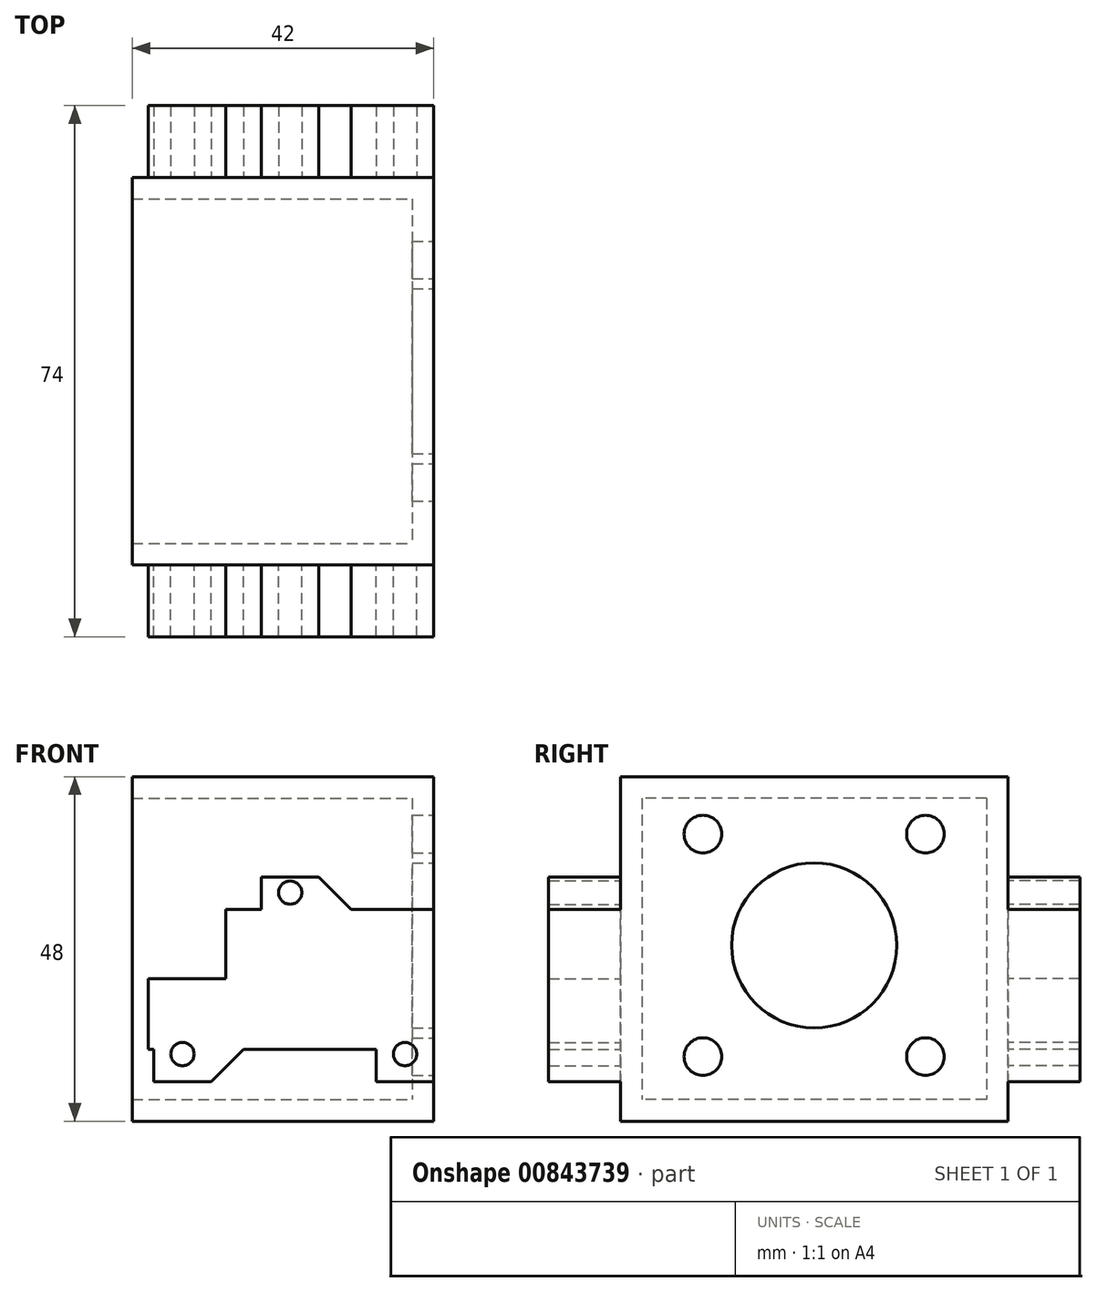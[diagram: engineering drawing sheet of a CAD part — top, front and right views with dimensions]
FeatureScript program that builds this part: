
annotation { "Feature Type Name" : "Feature", "Feature Type Description" : "" }
export const myFeature = defineFeature(function(context is Context, id is Id, definition is map)
    precondition{}
    {
        {
            var Q0;
            Q0=qCreatedBy(makeId("Front.planeOp"),FACE);
            var sketch = newSketch(context, id + "F0", { "sketchPlane" : qUnion([Q0])});
            skCircle(sketch, "E0", {"center": v(-1, 9.35) * mm, "radius": 1.63 * mm});
            skCircle(sketch, "E1", {"center": v(-32, 9.35) * mm, "radius": 1.63 * mm});
            skCircle(sketch, "E2", {"center": v(-17, 31.85) * mm, "radius": 1.63 * mm});
            skLineSegment(sketch, "E3", {"start": v(3, 5.5) * mm, "end": v(-5, 5.5) * mm});
            skLineSegment(sketch, "E4", {"start": v(-5, 5.5) * mm, "end": v(-5, 10) * mm});
            skLineSegment(sketch, "E5", {"start": v(-5, 10) * mm, "end": v(-23.5, 10) * mm});
            skLineSegment(sketch, "E6", {"start": v(-28, 5.5) * mm, "end": v(-28, 5.5) * mm});
            skLineSegment(sketch, "E7", {"start": v(-28, 5.5) * mm, "end": v(-36, 5.5) * mm});
            skLineSegment(sketch, "E8", {"start": v(-36, 5.5) * mm, "end": v(-36, 10) * mm});
            skLineSegment(sketch, "E9", {"start": v(-36, 10) * mm, "end": v(-36.75, 10) * mm});
            skLineSegment(sketch, "E10", {"start": v(-36.75, 10) * mm, "end": v(-36.75, 19.85) * mm});
            skLineSegment(sketch, "E11", {"start": v(-36.75, 19.85) * mm, "end": v(-26, 19.85) * mm});
            skLineSegment(sketch, "E12", {"start": v(-26, 19.85) * mm, "end": v(-26, 29.5) * mm});
            skLineSegment(sketch, "E13", {"start": v(-26, 29.5) * mm, "end": v(-21, 29.5) * mm});
            skLineSegment(sketch, "E14", {"start": v(-21, 29.5) * mm, "end": v(-21, 34) * mm});
            skLineSegment(sketch, "E15", {"start": v(-21, 34) * mm, "end": v(-13, 34) * mm});
            skLineSegment(sketch, "E16", {"start": v(-13, 34) * mm, "end": v(-13, 34) * mm});
            skLineSegment(sketch, "E17", {"start": v(-8.5, 29.5) * mm, "end": v(3, 29.5) * mm});
            skLineSegment(sketch, "E18", {"start": v(3, 29.5) * mm, "end": v(3, 19.85) * mm});
            skLineSegment(sketch, "E19", {"start": v(3, 19.85) * mm, "end": v(3, 19.85) * mm});
            skLineSegment(sketch, "E20", {"start": v(3, 19.85) * mm, "end": v(3, 10) * mm});
            skLineSegment(sketch, "E21", {"start": v(3, 10) * mm, "end": v(3, 10) * mm});
            skLineSegment(sketch, "E22", {"start": v(3, 10) * mm, "end": v(3, 5.5) * mm});
            skPoint(sketch, "E23.visualSharp", {"position": v(-13, 29.5) * mm});
            skPoint(sketch, "E24.visualSharp", {"position": v(-28, 10) * mm});
            skLineSegment(sketch, "E25", {"start": v(-13, 34) * mm, "end": v(-8.5, 29.5) * mm});
            skLineSegment(sketch, "E26", {"start": v(-28, 5.5) * mm, "end": v(-23.5, 10) * mm});
            skSolve(sketch);
        }
        {
            var Q0;
            Q0=makeQuery(id+"F0.imprint","IMPRINT",FACE,{"disambiguationData":[TD([[makeQuery(id+"F0.imprint","IMPRINT",EDGE,{"derivedFrom":sQuery(id+"F0.wireOp",EDGE,"E0")}),-1.0]])]});
            extrude(context, id + "F1", {"entities" : qUnion([Q0]), "depth" : 10 * mm, "offsetDistance" : 25 * mm});
        }
        {
            var Q0;
            Q0=makeQuery(id+"F1.opExtrude","SWEPT_FACE",FACE,{"disambiguationData":[OSD([sQuery(id+"F0.wireOp",EDGE,"E20")])]});
            var sketch = newSketch(context, id + "F2", { "sketchPlane" : qUnion([Q0])});
            skArc(sketch, "E27", {"start": v(-10.34, 10.86) * mm, "mid": v(-1, 19.85) * mm, "end": v(-10.34, 28.84) * mm});
            skLineSegment(sketch, "E28", {"start": v(-10.34, 10.86) * mm, "end": v(-10.34, 28.84) * mm});
            skSolve(sketch);
        }
        {
            var Q0;
            {var subQ0=sQuery(id+"F2.wireOp",EDGE,"E28");Q0=makeQuery(id+"F2.imprint","IMPRINT",FACE,{"disambiguationData":[TD([[makeQuery(id+"F2.imprint","IMPRINT",EDGE,{"derivedFrom":subQ0}),-1.0]])]});}
            var Q1;
            {var subQ1=sQuery(id+"F0.wireOp",EDGE,"E20");var subQ6=makeQuery(id+"F1.opExtrude","SWEPT_EDGE",EDGE,{"disambiguationData":[OSD([sQuery(id+"F0.wireOp",EDGE,"E19"),subQ1])]});Q1=makeQuery(id+"F2.imprint","IMPRINT",FACE,{"disambiguationData":[TD([[makeQuery(id+"F2.imprint","IMPRINT",EDGE,{"derivedFrom":subQ6}),-1.0]])]});}
            var Q2;
            {var subQ0=sQuery(id+"F2.wireOp",EDGE,"E27");var subQ1=makeQuery(id+"F1.opExtrude","CAP_EDGE",EDGE,{"disambiguationData":[OSD([sQuery(id+"F0.wireOp",EDGE,"E18"),sQuery(id+"F0.wireOp",EDGE,"E20"),sQuery(id+"F0.wireOp",EDGE,"E22")])],"isStart":false});var subQ2=makeQuery(id+"F2.imprint","INTERSECT",VERTEX,{"disambiguationData":[OD(0.0)],"derivedFrom":[subQ1,subQ0]});Q2=makeQuery(id+"F2.imprint","IMPRINT",FACE,{"disambiguationData":[TD([[makeQuery(id+"F2.imprint","IMPRINT",EDGE,{"disambiguationData":[TD([[subQ2,-1.0]])],"derivedFrom":subQ0}),1.0]])]});}
            extrude(context, id + "F3", {"entities" : qUnion([Q0, Q1, Q2]), "operationType" : NewBodyOperationType.REMOVE, "endBound" : BoundingType.THROUGH_ALL, "oppositeDirection" : true, "depth" : 25 * mm, "offsetDistance" : 25 * mm});
        }
        {
            var Q0;
            Q0=qCreatedBy(makeId("Top.planeOp"),FACE);
            var sketch = newSketch(context, id + "F4", { "sketchPlane" : qUnion([Q0])});
            skLineSegment(sketch, "E29.bottom", {"start": v(-39, 54) * mm, "end": v(3, 54) * mm});
            skLineSegment(sketch, "E29.top", {"start": v(-39, 0) * mm, "end": v(3, 0) * mm});
            skLineSegment(sketch, "E29.left", {"start": v(-39, 54) * mm, "end": v(-39, 0) * mm});
            skLineSegment(sketch, "E29.right", {"start": v(3, 54) * mm, "end": v(3, 0) * mm});
            skSolve(sketch);
        }
        {
            var Q0;
            Q0=makeQuery(id+"F4.imprint","IMPRINT",FACE,{"disambiguationData":[TD([[makeQuery(id+"F4.imprint","IMPRINT",EDGE,{"derivedFrom":sQuery(id+"F4.wireOp",EDGE,"E29.bottom")}),-1.0]])]});
            extrude(context, id + "F5", {"entities" : qUnion([Q0]), "depth" : 48 * mm, "offsetDistance" : 25 * mm});
        }
        {
            var Q0;
            Q0=makeQuery(id+"F5.opExtrude","SWEPT_FACE",FACE,{"disambiguationData":[OSD([sQuery(id+"F4.wireOp",EDGE,"E29.left")])]});
            shell(context, id + "F6", {"entities" : qUnion([Q0]), "thickness" : 3 * mm});
        }
        {
            var Q0;
            Q0=qCreatedBy(makeId("Front.planeOp"),FACE);
            cPlane(context, id + "F7", {"entities" : qUnion([Q0]), "cplaneType" : CPlaneType.OFFSET, "offset" : 27 * mm, "oppositeDirection" : true, "width" : 150 * mm, "height" : 150 * mm});
        }
        {
            var Q0;
            Q0=makeQuery(id+"F1.opExtrude","SWEPT_BODY",BODY,{"disambiguationData":[OSD([sQuery(id+"F0.wireOp",EDGE,"E0"),sQuery(id+"F0.wireOp",EDGE,"E1"),sQuery(id+"F0.wireOp",EDGE,"E2"),sQuery(id+"F0.wireOp",EDGE,"E3"),sQuery(id+"F0.wireOp",EDGE,"E4"),sQuery(id+"F0.wireOp",EDGE,"E5"),sQuery(id+"F0.wireOp",EDGE,"E6"),sQuery(id+"F0.wireOp",EDGE,"E7"),sQuery(id+"F0.wireOp",EDGE,"E8"),sQuery(id+"F0.wireOp",EDGE,"E9"),sQuery(id+"F0.wireOp",EDGE,"E10"),sQuery(id+"F0.wireOp",EDGE,"E11"),sQuery(id+"F0.wireOp",EDGE,"E12"),sQuery(id+"F0.wireOp",EDGE,"E13"),sQuery(id+"F0.wireOp",EDGE,"E14"),sQuery(id+"F0.wireOp",EDGE,"E15"),sQuery(id+"F0.wireOp",EDGE,"E16"),sQuery(id+"F0.wireOp",EDGE,"E17"),sQuery(id+"F0.wireOp",EDGE,"E18"),sQuery(id+"F0.wireOp",EDGE,"E19"),sQuery(id+"F0.wireOp",EDGE,"E20"),sQuery(id+"F0.wireOp",EDGE,"E21"),sQuery(id+"F0.wireOp",EDGE,"E22")])]});
            var Q1;
            Q1=qCreatedBy(id+"F7.planeOp",FACE);
            mirror(context, id + "F8", {"operationType" : NewBodyOperationType.ADD, "entities" : qUnion([Q0]), "mirrorPlane" : qUnion([Q1])});
        }
        {
            var Q0;
            Q0=makeQuery(id+"F5.opExtrude","SWEPT_FACE",FACE,{"disambiguationData":[OSD([sQuery(id+"F4.wireOp",EDGE,"E29.right")])]});
            var sketch = newSketch(context, id + "F9", { "sketchPlane" : qUnion([Q0])});
            skCircle(sketch, "E30", {"center": v(11.5, 40) * mm, "radius": 2.62 * mm});
            skCircle(sketch, "E31", {"center": v(42.5, 40) * mm, "radius": 2.62 * mm});
            skCircle(sketch, "E32", {"center": v(42.5, 9) * mm, "radius": 2.62 * mm});
            skCircle(sketch, "E33", {"center": v(11.5, 9) * mm, "radius": 2.62 * mm});
            skLineSegment(sketch, "E34", {"start": v(11.5, 40) * mm, "end": v(42.5, 9) * mm, "construction": true});
            skLineSegment(sketch, "E35", {"start": v(11.5, 9) * mm, "end": v(42.5, 40) * mm, "construction": true});
            skCircle(sketch, "E36", {"center": v(27, 24.5) * mm, "radius": 11.5 * mm});
            skSolve(sketch);
        }
        {
            var Q0;
            Q0=makeQuery(id+"F9.imprint","IMPRINT",FACE,{"disambiguationData":[TD([[makeQuery(id+"F9.imprint","IMPRINT",EDGE,{"derivedFrom":sQuery(id+"F9.wireOp",EDGE,"E30")}),1.0]])]});
            var Q1;
            Q1=makeQuery(id+"F9.imprint","IMPRINT",FACE,{"disambiguationData":[TD([[makeQuery(id+"F9.imprint","IMPRINT",EDGE,{"derivedFrom":sQuery(id+"F9.wireOp",EDGE,"E36")}),1.0]])]});
            var Q2;
            Q2=makeQuery(id+"F9.imprint","IMPRINT",FACE,{"disambiguationData":[TD([[makeQuery(id+"F9.imprint","IMPRINT",EDGE,{"derivedFrom":sQuery(id+"F9.wireOp",EDGE,"E33")}),1.0]])]});
            var Q3;
            Q3=makeQuery(id+"F9.imprint","IMPRINT",FACE,{"disambiguationData":[TD([[makeQuery(id+"F9.imprint","IMPRINT",EDGE,{"derivedFrom":sQuery(id+"F9.wireOp",EDGE,"E32")}),1.0]])]});
            var Q4;
            Q4=makeQuery(id+"F9.imprint","IMPRINT",FACE,{"disambiguationData":[TD([[makeQuery(id+"F9.imprint","IMPRINT",EDGE,{"derivedFrom":sQuery(id+"F9.wireOp",EDGE,"E31")}),1.0]])]});
            extrude(context, id + "F10", {"entities" : qUnion([Q0, Q1, Q2, Q3, Q4]), "operationType" : NewBodyOperationType.REMOVE, "endBound" : BoundingType.THROUGH_ALL, "oppositeDirection" : true, "depth" : 25 * mm, "offsetDistance" : 25 * mm});
        }
    });
